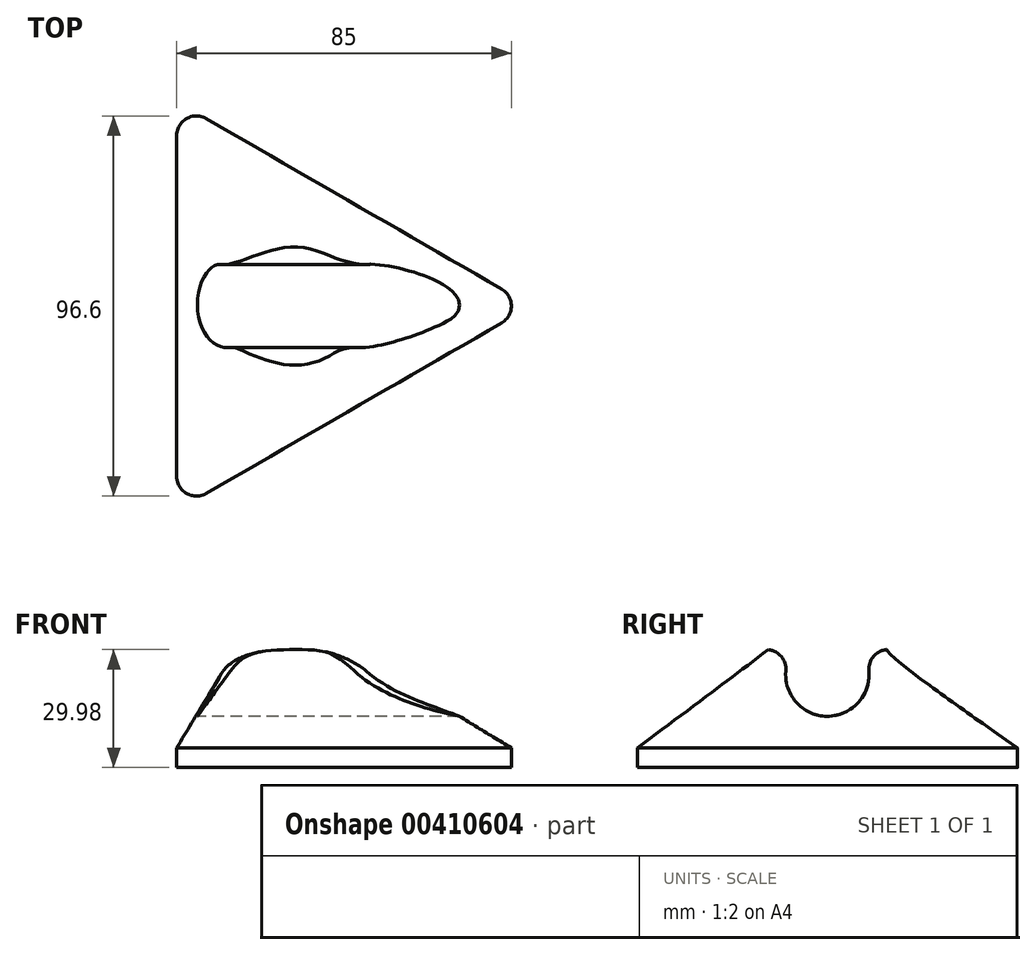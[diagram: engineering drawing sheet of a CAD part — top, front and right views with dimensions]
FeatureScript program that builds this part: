
annotation { "Feature Type Name" : "Feature", "Feature Type Description" : "" }
export const myFeature = defineFeature(function(context is Context, id is Id, definition is map)
    precondition{}
    {
        {
            var Q0;
            Q0=qCreatedBy(makeId("Top.planeOp"),FACE);
            var sketch = newSketch(context, id + "F0", { "sketchPlane" : qUnion([Q0])});
            skCircle(sketch, "E0.cCircle", {"center": v(0, 0) * mm, "radius": 60 * mm, "construction": true});
            skLineSegment(sketch, "E0.0", {"start": v(52.5, -4.33) * mm, "end": v(-22.5, -47.63) * mm});
            skLineSegment(sketch, "E0.1", {"start": v(-30, -43.3) * mm, "end": v(-30, 43.3) * mm});
            skLineSegment(sketch, "E0.2", {"start": v(-22.5, 47.63) * mm, "end": v(52.5, 4.33) * mm});
            skPoint(sketch, "E1.visualSharp", {"position": v(-30, 51.96) * mm});
            skArc(sketch, "E1.filletArc", {"start": v(-22.5, 47.63) * mm, "mid": v(-27.5, 47.63) * mm, "end": v(-30, 43.3) * mm});
            skPoint(sketch, "E2.visualSharp", {"position": v(-30, -51.96) * mm});
            skArc(sketch, "E2.filletArc", {"start": v(-30, -43.3) * mm, "mid": v(-27.5, -47.63) * mm, "end": v(-22.5, -47.63) * mm});
            skPoint(sketch, "E3.visualSharp", {"position": v(60, 0) * mm});
            skArc(sketch, "E3.filletArc", {"start": v(52.5, -4.33) * mm, "mid": v(55, 0) * mm, "end": v(52.5, 4.33) * mm});
            skCircle(sketch, "E4", {"center": v(0, 0) * mm, "radius": 15 * mm});
            skSolve(sketch);
        }
        {
            var Q0;
            Q0=makeQuery(id+"F0.imprint","IMPRINT",FACE,{"disambiguationData":[TD([[makeQuery(id+"F0.imprint","IMPRINT",EDGE,{"derivedFrom":sQuery(id+"F0.wireOp",EDGE,"E0.0")}),-1.0]])]});
            extrude(context, id + "F1", {"entities" : qUnion([Q0]), "depth" : 5 * mm});
        }
        {
            var Q0;
            Q0=makeQuery(id+"F0.imprint","IMPRINT",FACE,{"disambiguationData":[TD([[makeQuery(id+"F0.imprint","IMPRINT",EDGE,{"derivedFrom":sQuery(id+"F0.wireOp",EDGE,"E4")}),1.0]])]});
            extrude(context, id + "F2", {"entities" : qUnion([Q0]), "operationType" : NewBodyOperationType.ADD, "depth" : 30 * mm});
        }
        {
            var Q0;
            Q0=makeQuery(id+"F1.opExtrude","CAP_FACE",FACE,{"disambiguationData":[OSD([sQuery(id+"F0.wireOp",EDGE,"E0.0"),sQuery(id+"F0.wireOp",EDGE,"E0.1"),sQuery(id+"F0.wireOp",EDGE,"E0.2"),sQuery(id+"F0.wireOp",EDGE,"E1.filletArc"),sQuery(id+"F0.wireOp",EDGE,"E2.filletArc"),sQuery(id+"F0.wireOp",EDGE,"E3.filletArc"),sQuery(id+"F0.wireOp",EDGE,"E4")])],"isStart":false});
            cPlane(context, id + "F3", {"entities" : qUnion([Q0]), "cplaneType" : CPlaneType.OFFSET, "offset" : 0 * mm, "width" : 150 * mm, "height" : 150 * mm});
        }
        {
            var Q0;
            Q0=qCreatedBy(id+"F3.planeOp",FACE);
            var sketch = newSketch(context, id + "F4", { "sketchPlane" : qUnion([Q0])});
            skLineSegment(sketch, "E5.0", {"start": v(52.5, -4.33) * mm, "end": v(-22.5, -47.63) * mm});
            skArc(sketch, "E5.1", {"start": v(-30, -43.3) * mm, "mid": v(-27.5, -47.63) * mm, "end": v(-22.5, -47.63) * mm});
            skLineSegment(sketch, "E5.2", {"start": v(-30, -43.3) * mm, "end": v(-30, 43.3) * mm});
            skArc(sketch, "E5.3", {"start": v(-22.5, 47.63) * mm, "mid": v(-27.5, 47.63) * mm, "end": v(-30, 43.3) * mm});
            skLineSegment(sketch, "E5.4", {"start": v(-22.5, 47.63) * mm, "end": v(52.5, 4.33) * mm});
            skArc(sketch, "E5.5", {"start": v(52.5, -4.33) * mm, "mid": v(55, 0) * mm, "end": v(52.5, 4.33) * mm});
            skSolve(sketch);
        }
        {
            var Q1;
            Q1=makeQuery(id+"F4.imprint","IMPRINT",FACE,{"disambiguationData":[TD([[makeQuery(id+"F4.imprint","IMPRINT",EDGE,{"derivedFrom":sQuery(id+"F4.wireOp",EDGE,"E5.0")}),-1.0]])]});
            var Q2;
            Q2=makeQuery(id+"F2.opExtrude","CAP_FACE",FACE,{"disambiguationData":[OSD([sQuery(id+"F0.wireOp",EDGE,"E4")])],"isStart":false});
            loft(context, id + "F5", {"operationType" : NewBodyOperationType.ADD, "sheetProfilesArray" : [{ "sheetProfileEntities" : qUnion([Q1]) }, { "sheetProfileEntities" : qUnion([Q2]) }]});
        }
        {
            var Q0;
            Q0=qCreatedBy(makeId("Right.planeOp"),FACE);
            var sketch = newSketch(context, id + "F6", { "sketchPlane" : qUnion([Q0])});
            skFitSpline(sketch, "E6.0", {"points": [v(-13.56, 30) * mm, v(-9.45, 30) * mm, v(-5.34, 30) * mm, v(-1.23, 30) * mm], "construction": true});
            skFitSpline(sketch, "E6.1", {"points": [v(-1.23, 30) * mm, v(3.29, 30) * mm, v(7.81, 30) * mm, v(12.33, 30) * mm], "construction": true});
            skFitSpline(sketch, "E6.2", {"points": [v(12.33, 30) * mm, v(13.22, 30) * mm, v(14.11, 30) * mm, v(15, 30) * mm], "construction": true});
            skFitSpline(sketch, "E6.3", {"points": [v(13.56, 30) * mm, v(9.45, 30) * mm, v(5.34, 30) * mm, v(1.23, 30) * mm], "construction": true});
            skFitSpline(sketch, "E6.4", {"points": [v(-12.33, 30) * mm, v(-13.22, 30) * mm, v(-14.11, 30) * mm, v(-15, 30) * mm], "construction": true});
            skFitSpline(sketch, "E6.5", {"points": [v(1.23, 30) * mm, v(-3.29, 30) * mm, v(-7.81, 30) * mm, v(-12.33, 30) * mm], "construction": true});
            skPoint(sketch, "E7", {"position": v(0, 30) * mm});
            skLineSegment(sketch, "E8", {"start": v(0, 30) * mm, "end": v(0, 13.04) * mm, "construction": true});
            skPoint(sketch, "E9", {"position": v(0, 23.64) * mm});
            skCircle(sketch, "E10", {"center": v(0, 23.64) * mm, "radius": 10.6 * mm});
            skSolve(sketch);
        }
        {
            var Q0;
            Q0 = qSketchRegion(id + "F6", true);
            extrude(context, id + "F7", {"entities" : qUnion([Q0]), "operationType" : NewBodyOperationType.REMOVE, "endBound" : BoundingType.SYMMETRIC, "depth" : 150 * mm});
        }
        {
            var Q0;
            Q0=makeQuery(id+"F7.boolean.opBoolean","INTERSECT",EDGE,{"disambiguationData":[OD(1.0)],"derivedFrom":[makeQuery(id+"F2.opExtrude","CAP_FACE",FACE,{"disambiguationData":[OSD([sQuery(id+"F0.wireOp",EDGE,"E4")])],"isStart":false}),makeQuery(id+"F7.opExtrude","SWEPT_FACE",FACE,{"disambiguationData":[OSD([sQuery(id+"F6.wireOp",EDGE,"E10")])]})]});
            var Q1;
            Q1=makeQuery(id+"F7.boolean.opBoolean","INTERSECT",EDGE,{"disambiguationData":[OD(0.0)],"derivedFrom":[makeQuery(id+"F2.opExtrude","CAP_FACE",FACE,{"disambiguationData":[OSD([sQuery(id+"F0.wireOp",EDGE,"E4")])],"isStart":false}),makeQuery(id+"F7.opExtrude","SWEPT_FACE",FACE,{"disambiguationData":[OSD([sQuery(id+"F6.wireOp",EDGE,"E10")])]})]});
            fillet(context, id + "F8", {"entities" : qUnion([Q0, Q1]), "radius" : 5 * mm, "tangentPropagation" : true, "allowEdgeOverflow" : false});
        }
    });
